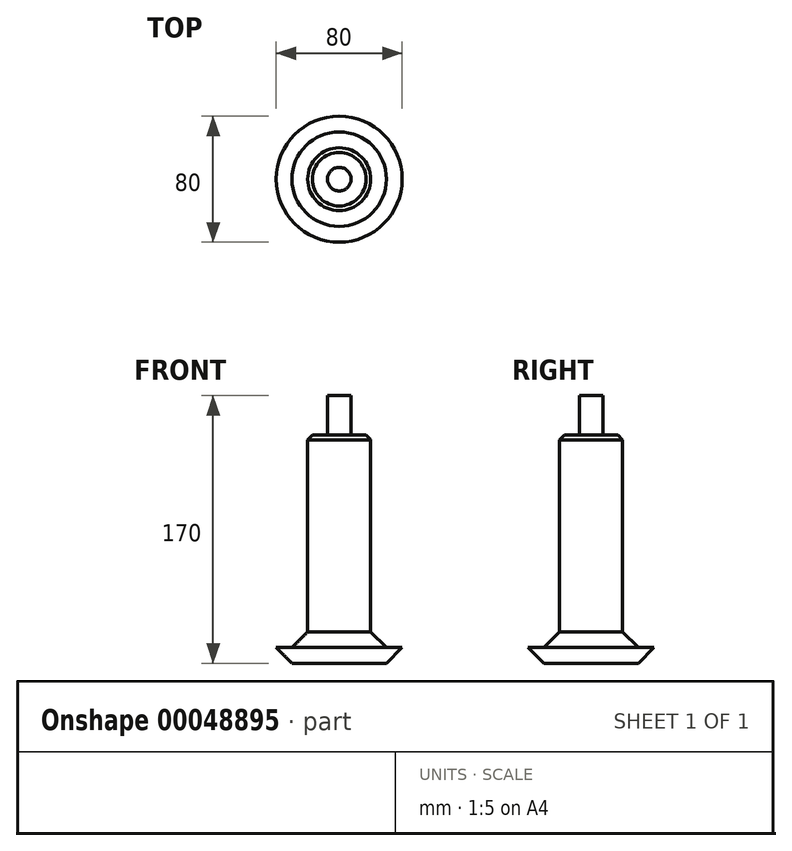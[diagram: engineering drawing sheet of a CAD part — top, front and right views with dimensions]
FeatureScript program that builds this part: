
annotation { "Feature Type Name" : "Feature", "Feature Type Description" : "" }
export const myFeature = defineFeature(function(context is Context, id is Id, definition is map)
    precondition{}
    {
        {
            var Q0;
            Q0=qCreatedBy(makeId("Top.planeOp"),FACE);
            var sketch = newSketch(context, id + "F0", { "sketchPlane" : qUnion([Q0])});
            skCircle(sketch, "E0", {"center": v(0, 0) * mm, "radius": 20 * mm});
            skSolve(sketch);
        }
        {
            var Q0;
            Q0=makeQuery(id+"F0.imprint","IMPRINT",FACE,{"disambiguationData":[TD([[makeQuery(id+"F0.imprint","IMPRINT",EDGE,{"derivedFrom":sQuery(id+"F0.wireOp",EDGE,"E0")}),1.0]])]});
            extrude(context, id + "F1", {"entities" : qUnion([Q0]), "depth" : 125 * mm});
        }
        {
            var Q0;
            Q0=makeQuery(id+"F1.opExtrude","CAP_FACE",FACE,{"disambiguationData":[OSD([sQuery(id+"F0.wireOp",EDGE,"E0")])],"isStart":false});
            var sketch = newSketch(context, id + "F2", { "sketchPlane" : qUnion([Q0])});
            skCircle(sketch, "E1", {"center": v(0, 0) * mm, "radius": 7.5 * mm});
            skSolve(sketch);
        }
        {
            var Q0;
            Q0 = qSketchRegion(id + "F2", true);
            extrude(context, id + "F3", {"entities" : qUnion([Q0]), "operationType" : NewBodyOperationType.ADD, "depth" : 25 * mm});
        }
        {
            var Q0;
            Q0=makeQuery(id+"F1.opExtrude","CAP_FACE",FACE,{"disambiguationData":[OSD([sQuery(id+"F0.wireOp",EDGE,"E0")])],"isStart":true});
            var sketch = newSketch(context, id + "F4", { "sketchPlane" : qUnion([Q0])});
            skCircle(sketch, "E2", {"center": v(0, 0) * mm, "radius": 20 * mm});
            skSolve(sketch);
        }
        {
            var Q0;
            Q0=makeQuery(id+"F4.imprint","IMPRINT",FACE,{"disambiguationData":[TD([[makeQuery(id+"F4.imprint","IMPRINT",EDGE,{"derivedFrom":sQuery(id+"F4.wireOp",EDGE,"E2")}),-1.0]])]});
            extrude(context, id + "F5", {"entities" : qUnion([Q0]), "operationType" : NewBodyOperationType.ADD, "depth" : 10 * mm, "hasDraft" : true, "draftAngle" : 45 * degree});
        }
        {
            var Q0;
            Q0=makeQuery(id+"F5.opExtrude","CAP_FACE",FACE,{"disambiguationData":[OSD([sQuery(id+"F4.wireOp",EDGE,"E2")])],"isStart":false});
            var sketch = newSketch(context, id + "F6", { "sketchPlane" : qUnion([Q0])});
            skCircle(sketch, "E3", {"center": v(0, 0) * mm, "radius": 40 * mm});
            skSolve(sketch);
        }
        {
            var Q0;
            Q0=makeQuery(id+"F6.imprint","IMPRINT",FACE,{"disambiguationData":[TD([[makeQuery(id+"F6.imprint","IMPRINT",EDGE,{"derivedFrom":sQuery(id+"F6.wireOp",EDGE,"E3")}),1.0]])]});
            var Q1;
            Q1=makeQuery(id+"F6.imprint","IMPRINT",FACE,{"disambiguationData":[TD([[makeQuery(id+"F6.imprint","IMPRINT",EDGE,{"derivedFrom":makeQuery(id+"F5.opExtrude","CAP_EDGE",EDGE,{"disambiguationData":[OSD([sQuery(id+"F4.wireOp",EDGE,"E2")])],"isStart":false})}),-1.0]])]});
            extrude(context, id + "F7", {"entities" : qUnion([Q0, Q1]), "operationType" : NewBodyOperationType.ADD, "depth" : 10 * mm, "hasDraft" : true, "draftAngle" : 45 * degree, "draftPullDirection" : true});
        }
        {
            var Q0;
            Q0=makeQuery(id+"F1.opExtrude","CAP_EDGE",EDGE,{"disambiguationData":[OSD([sQuery(id+"F0.wireOp",EDGE,"E0")])],"isStart":false});
            chamfer(context, id + "F8", {"entities" : qUnion([Q0]), "chamferType" : ChamferType.OFFSET_ANGLE, "width" : 3 * mm, "oppositeDirection" : false, "angle" : 45 * degree, "tangentPropagation" : true});
        }
    });
